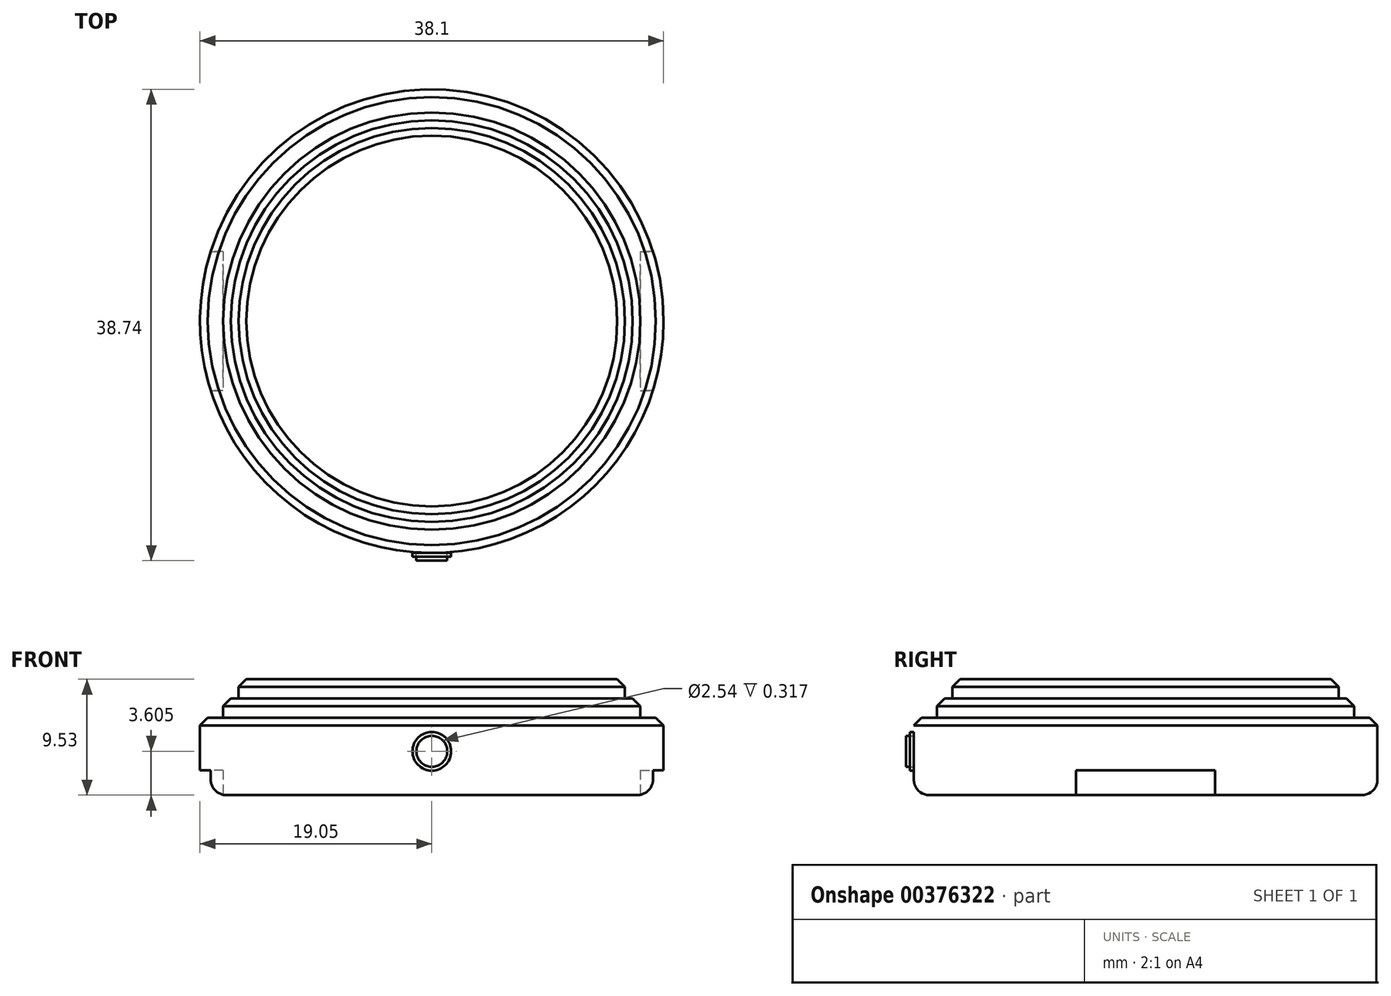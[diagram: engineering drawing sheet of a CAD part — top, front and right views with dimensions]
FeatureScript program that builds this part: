
annotation { "Feature Type Name" : "Feature", "Feature Type Description" : "" }
export const myFeature = defineFeature(function(context is Context, id is Id, definition is map)
    precondition{}
    {
        {
            var Q0;
            Q0=qCreatedBy(makeId("Top.planeOp"),FACE);
            var sketch = newSketch(context, id + "F0", { "sketchPlane" : qUnion([Q0])});
            skCircle(sketch, "E0", {"center": v(0, 0) * mm, "radius": 19.05 * mm});
            skSolve(sketch);
        }
        {
            var Q0;
            Q0=makeQuery(id+"F0.imprint","IMPRINT",FACE,{"disambiguationData":[TD([[makeQuery(id+"F0.imprint","IMPRINT",EDGE,{"derivedFrom":sQuery(id+"F0.wireOp",EDGE,"E0")}),1.0]])]});
            extrude(context, id + "F1", {"entities" : qUnion([Q0]), "depth" : 6.35 * mm});
        }
        {
            var Q0;
            Q0=makeQuery(id+"F1.opExtrude","CAP_FACE",FACE,{"disambiguationData":[OSD([sQuery(id+"F0.wireOp",EDGE,"E0")])],"isStart":false});
            var sketch = newSketch(context, id + "F2", { "sketchPlane" : qUnion([Q0])});
            skCircle(sketch, "E1", {"center": v(0, 0) * mm, "radius": 17.15 * mm});
            skCircle(sketch, "E2", {"center": v(0, 0) * mm, "radius": 15.88 * mm});
            skSolve(sketch);
        }
        {
            var Q0;
            Q0=makeQuery(id+"F2.imprint","IMPRINT",FACE,{"disambiguationData":[TD([[makeQuery(id+"F2.imprint","IMPRINT",EDGE,{"derivedFrom":sQuery(id+"F2.wireOp",EDGE,"E1")}),1.0]])]});
            extrude(context, id + "F3", {"entities" : qUnion([Q0]), "operationType" : NewBodyOperationType.ADD, "depth" : 1.59 * mm});
        }
        {
            var Q0;
            Q0=makeQuery(id+"F3.boolean.opBoolean","SPLIT",FACE,{"disambiguationData":[TD([makeQuery(id+"F3.opExtrude","SWEPT_FACE",FACE,{"disambiguationData":[OSD([sQuery(id+"F2.wireOp",EDGE,"E2")])]})])],"derivedFrom":makeQuery(id+"F1.opExtrude","CAP_FACE",FACE,{"disambiguationData":[OSD([sQuery(id+"F0.wireOp",EDGE,"E0")])],"isStart":false})});
            extrude(context, id + "F4", {"entities" : qUnion([Q0]), "operationType" : NewBodyOperationType.ADD, "depth" : 3.17 * mm});
        }
        {
            var Q0;
            Q0=makeQuery(id+"F1.opExtrude","CAP_EDGE",EDGE,{"disambiguationData":[OSD([sQuery(id+"F0.wireOp",EDGE,"E0")])],"isStart":false});
            var Q1;
            Q1=makeQuery(id+"F3.opExtrude","CAP_EDGE",EDGE,{"disambiguationData":[OSD([sQuery(id+"F2.wireOp",EDGE,"E1")])],"isStart":false});
            var Q2;
            Q2=makeQuery(id+"F4.opExtrude","CAP_EDGE",EDGE,{"disambiguationData":[OSD([sQuery(id+"F2.wireOp",EDGE,"E2")])],"isStart":false});
            chamfer(context, id + "F5", {"entities" : qUnion([Q0, Q1, Q2]), "width" : 0.64 * mm, "tangentPropagation" : true});
        }
        {
            var Q0;
            Q0=makeQuery(id+"F1.opExtrude","CAP_EDGE",EDGE,{"disambiguationData":[OSD([sQuery(id+"F0.wireOp",EDGE,"E0")])],"isStart":true});
            fillet(context, id + "F6", {"entities" : qUnion([Q0]), "radius" : 1.27 * mm, "tangentPropagation" : true, "allowEdgeOverflow" : false});
        }
        {
            var Q0;
            Q0=qCreatedBy(makeId("Front.planeOp"),FACE);
            cPlane(context, id + "F7", {"entities" : qUnion([Q0]), "cplaneType" : CPlaneType.OFFSET, "offset" : 19.05 * mm, "width" : 152.4 * mm, "height" : 152.4 * mm});
        }
        {
            var Q0;
            Q0=qCreatedBy(id+"F7.planeOp",FACE);
            var sketch = newSketch(context, id + "F8", { "sketchPlane" : qUnion([Q0])});
            skCircle(sketch, "E3", {"center": v(0, 3.6) * mm, "radius": 1.59 * mm});
            skCircle(sketch, "E4", {"center": v(0, 3.6) * mm, "radius": 1.27 * mm});
            skSolve(sketch);
        }
        {
            var Q0;
            Q0=makeQuery(id+"F8.imprint","IMPRINT",FACE,{"disambiguationData":[TD([[makeQuery(id+"F8.imprint","IMPRINT",EDGE,{"derivedFrom":sQuery(id+"F8.wireOp",EDGE,"E4")}),1.0]])]});
            extrude(context, id + "F9", {"entities" : qUnion([Q0]), "operationType" : NewBodyOperationType.ADD, "depth" : 0.64 * mm});
        }
        {
            var Q0;
            Q0=makeQuery(id+"F8.imprint","IMPRINT",FACE,{"disambiguationData":[TD([[makeQuery(id+"F8.imprint","IMPRINT",EDGE,{"derivedFrom":sQuery(id+"F8.wireOp",EDGE,"E3")}),1.0]])]});
            extrude(context, id + "F10", {"entities" : qUnion([Q0]), "depth" : 0.32 * mm});
        }
        {
            var Q0;
            Q0=qCreatedBy(makeId("Right.planeOp"),FACE);
            cPlane(context, id + "F11", {"entities" : qUnion([Q0]), "cplaneType" : CPlaneType.OFFSET, "offset" : 19.05 * mm, "width" : 152.4 * mm, "height" : 152.4 * mm});
        }
        {
            var Q0;
            Q0=qCreatedBy(id+"F11.planeOp",FACE);
            var sketch = newSketch(context, id + "F12", { "sketchPlane" : qUnion([Q0])});
            skLineSegment(sketch, "E5.bottom", {"start": v(5.72, 2.03) * mm, "end": v(-5.72, 2.03) * mm});
            skLineSegment(sketch, "E5.top", {"start": v(5.72, -2.03) * mm, "end": v(-5.72, -2.03) * mm});
            skLineSegment(sketch, "E5.left", {"start": v(5.72, 2.03) * mm, "end": v(5.72, -2.03) * mm});
            skLineSegment(sketch, "E5.right", {"start": v(-5.72, 2.03) * mm, "end": v(-5.72, -2.03) * mm});
            skPoint(sketch, "E5.middle", {"position": v(0, 0) * mm});
            skSolve(sketch);
        }
        {
            var Q0;
            Q0=makeQuery(id+"F12.imprint","IMPRINT",FACE,{"disambiguationData":[TD([[makeQuery(id+"F12.imprint","IMPRINT",EDGE,{"derivedFrom":sQuery(id+"F12.wireOp",EDGE,"E5.bottom")}),1.0]])]});
            extrude(context, id + "F13", {"entities" : qUnion([Q0]), "operationType" : NewBodyOperationType.REMOVE, "oppositeDirection" : true, "depth" : 1.9 * mm});
        }
        {
            var Q0;
            Q0=qCreatedBy(makeId("Right.planeOp"),FACE);
            cPlane(context, id + "F14", {"entities" : qUnion([Q0]), "cplaneType" : CPlaneType.OFFSET, "offset" : 19.05 * mm, "oppositeDirection" : true, "width" : 152.4 * mm, "height" : 152.4 * mm});
        }
        {
            var Q0;
            Q0=qCreatedBy(id+"F14.planeOp",FACE);
            var sketch = newSketch(context, id + "F15", { "sketchPlane" : qUnion([Q0])});
            skLineSegment(sketch, "E6.bottom", {"start": v(5.72, 2.03) * mm, "end": v(-5.72, 2.03) * mm});
            skLineSegment(sketch, "E6.top", {"start": v(5.72, -2.03) * mm, "end": v(-5.72, -2.03) * mm});
            skLineSegment(sketch, "E6.left", {"start": v(5.72, 2.03) * mm, "end": v(5.72, -2.03) * mm});
            skLineSegment(sketch, "E6.right", {"start": v(-5.72, 2.03) * mm, "end": v(-5.72, -2.03) * mm});
            skPoint(sketch, "E6.middle", {"position": v(0, 0) * mm});
            skSolve(sketch);
        }
        {
            var Q0;
            Q0=makeQuery(id+"F15.imprint","IMPRINT",FACE,{"disambiguationData":[TD([[makeQuery(id+"F15.imprint","IMPRINT",EDGE,{"derivedFrom":sQuery(id+"F15.wireOp",EDGE,"E6.bottom")}),1.0]])]});
            extrude(context, id + "F16", {"entities" : qUnion([Q0]), "operationType" : NewBodyOperationType.REMOVE, "depth" : 1.9 * mm});
        }
    });
